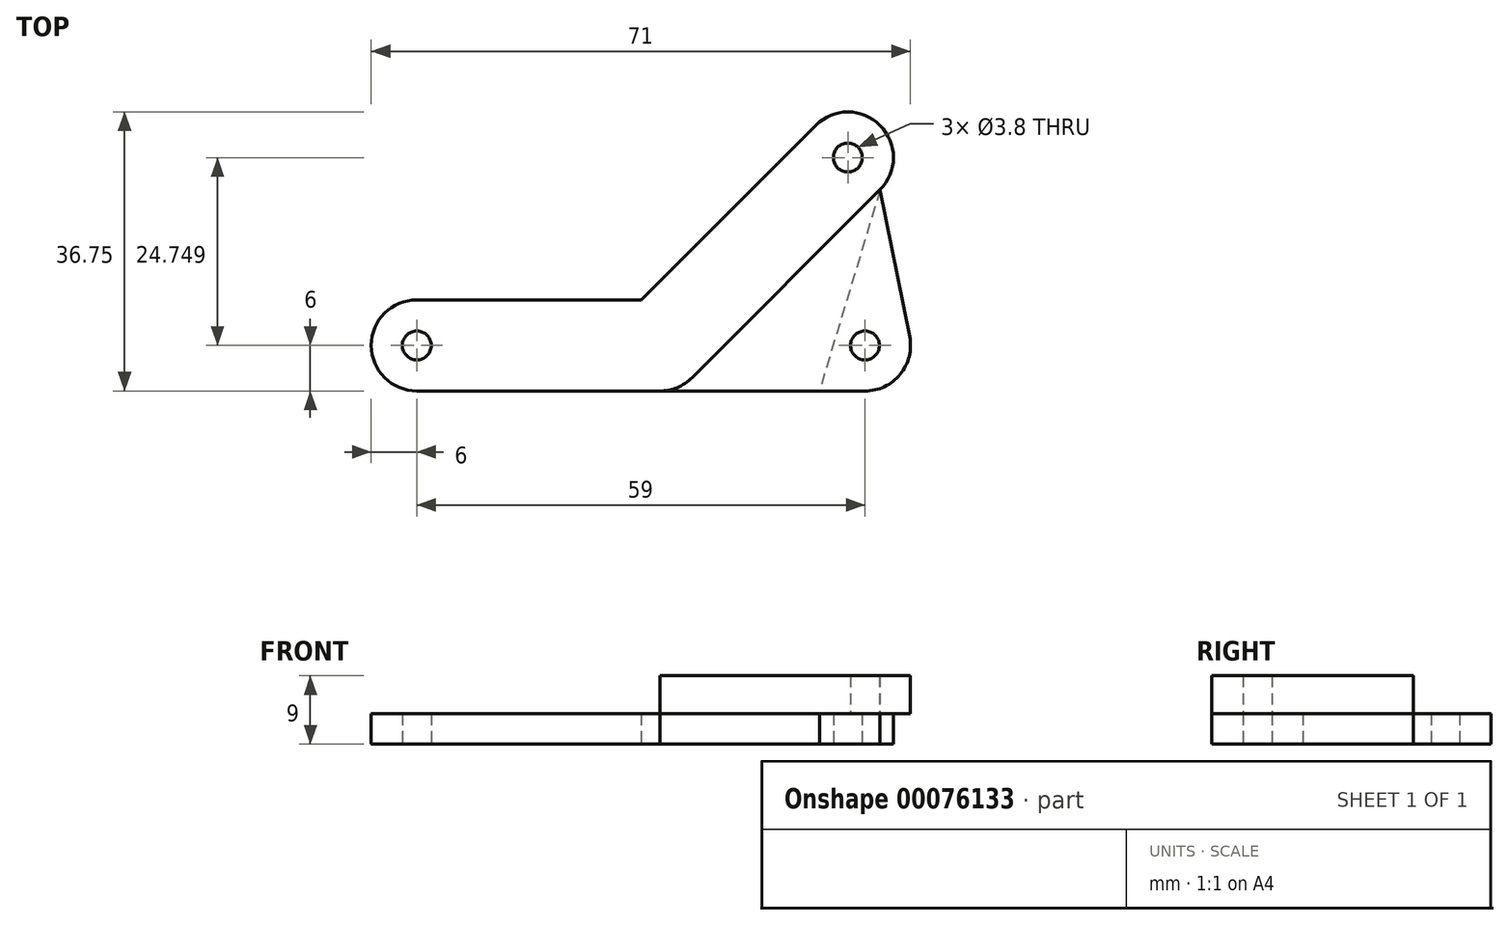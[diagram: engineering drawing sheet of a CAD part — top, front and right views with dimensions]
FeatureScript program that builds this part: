
annotation { "Feature Type Name" : "Feature", "Feature Type Description" : "" }
export const myFeature = defineFeature(function(context is Context, id is Id, definition is map)
    precondition{}
    {
        {
            var Q0;
            Q0=qCreatedBy(makeId("Top.planeOp"),FACE);
            var sketch = newSketch(context, id + "F0", { "sketchPlane" : qUnion([Q0])});
            skLineSegment(sketch, "E0", {"start": v(0, 0) * mm, "end": v(-32, 0) * mm});
            skCircle(sketch, "E1", {"center": v(-32, 0) * mm, "radius": 6 * mm});
            skLineSegment(sketch, "E2", {"start": v(0, 0) * mm, "end": v(24.75, 24.75) * mm});
            skCircle(sketch, "E3", {"center": v(24.75, 24.75) * mm, "radius": 6 * mm});
            skLineSegment(sketch, "E4", {"start": v(-32, 6) * mm, "end": v(0, 6) * mm});
            skLineSegment(sketch, "E5", {"start": v(-32, -6) * mm, "end": v(0, -6) * mm});
            skLineSegment(sketch, "E6", {"start": v(20.5, 29) * mm, "end": v(-4.24, 4.24) * mm});
            skLineSegment(sketch, "E7", {"start": v(4.24, -4.24) * mm, "end": v(29, 20.5) * mm});
            skCircle(sketch, "E8", {"center": v(-32, 0) * mm, "radius": 1.9 * mm});
            skCircle(sketch, "E9", {"center": v(24.75, 24.75) * mm, "radius": 1.9 * mm});
            skArc(sketch, "E10", {"start": v(0, -6) * mm, "mid": v(2.3, -5.54) * mm, "end": v(4.24, -4.24) * mm});
            skArc(sketch, "E11", {"start": v(4.24, -4.24) * mm, "mid": v(-2.3, 5.54) * mm, "end": v(0, -6) * mm, "construction": true});
            skSolve(sketch);
        }
        {
            var Q0;
            Q0 = qSketchRegion(id + "F0", true);
            extrude(context, id + "F1", {"entities" : qUnion([Q0]), "depth" : 4 * mm});
        }
        {
            var Q0;
            Q0=makeQuery(id+"F1.opExtrude","CAP_FACE",FACE,{"disambiguationData":[OSD([sQuery(id+"F0.wireOp",EDGE,"E1"),sQuery(id+"F0.wireOp",EDGE,"E3"),sQuery(id+"F0.wireOp",EDGE,"E4"),sQuery(id+"F0.wireOp",EDGE,"E5"),sQuery(id+"F0.wireOp",EDGE,"E6"),sQuery(id+"F0.wireOp",EDGE,"E7"),sQuery(id+"F0.wireOp",EDGE,"E8"),sQuery(id+"F0.wireOp",EDGE,"E9"),sQuery(id+"F0.wireOp",EDGE,"E10")])],"isStart":false});
            var sketch = newSketch(context, id + "F2", { "sketchPlane" : qUnion([Q0])});
            skLineSegment(sketch, "E12", {"start": v(0, 0) * mm, "end": v(27, 0) * mm, "construction": true});
            skLineSegment(sketch, "E13.0", {"start": v(4.24, -4.24) * mm, "end": v(29, 20.5) * mm});
            skLineSegment(sketch, "E14", {"start": v(29, 20.5) * mm, "end": v(32.88, 1.18) * mm});
            skArc(sketch, "E15.0", {"start": v(0, -6) * mm, "mid": v(2.3, -5.54) * mm, "end": v(4.24, -4.24) * mm});
            skLineSegment(sketch, "E16", {"start": v(0, -6) * mm, "end": v(27, -6) * mm});
            skCircle(sketch, "E17", {"center": v(27, 0) * mm, "radius": 1.9 * mm});
            skArc(sketch, "E18", {"start": v(32.88, 1.18) * mm, "mid": v(22.36, 3.8) * mm, "end": v(27, -6) * mm, "construction": true});
            skArc(sketch, "E19", {"start": v(27, -6) * mm, "mid": v(31.64, -3.8) * mm, "end": v(32.88, 1.18) * mm});
            skSolve(sketch);
        }
        {
            var Q0;
            Q0 = qSketchRegion(id + "F2", true);
            extrude(context, id + "F3", {"entities" : qUnion([Q0]), "depth" : 5 * mm});
        }
        {
            var Q0;
            Q0=makeQuery(id+"F3.opExtrude","CAP_FACE",FACE,{"disambiguationData":[OSD([sQuery(id+"F2.wireOp",EDGE,"E13.0"),sQuery(id+"F2.wireOp",EDGE,"E14"),sQuery(id+"F2.wireOp",EDGE,"E15.0"),sQuery(id+"F2.wireOp",EDGE,"E16"),sQuery(id+"F2.wireOp",EDGE,"E17"),sQuery(id+"F2.wireOp",EDGE,"E19")])],"isStart":true});
            var sketch = newSketch(context, id + "F4", { "sketchPlane" : qUnion([Q0])});
            skLineSegment(sketch, "E20.0", {"start": v(4.24, 4.24) * mm, "end": v(29, -20.5) * mm});
            skArc(sketch, "E21.0", {"start": v(0, 6) * mm, "mid": v(2.3, 5.54) * mm, "end": v(4.24, 4.24) * mm});
            skLineSegment(sketch, "E22.0", {"start": v(0, 6) * mm, "end": v(21, 6) * mm});
            skLineSegment(sketch, "E23", {"start": v(29, -20.5) * mm, "end": v(21, 6) * mm});
            skSolve(sketch);
        }
        {
            var Q0;
            Q0 = qSketchRegion(id + "F4", true);
            extrude(context, id + "F5", {"entities" : qUnion([Q0]), "depth" : 4 * mm});
        }
    });
